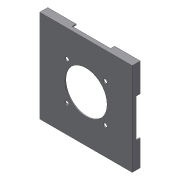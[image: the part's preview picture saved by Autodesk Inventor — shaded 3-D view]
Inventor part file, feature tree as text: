
AUTODESK INVENTOR PART (.ipt)
format: ipt  version: 2017 (Build 210142000, 142)  size: 223,744 bytes
history: native  units: mm
features: sketch x7, extrude x5, projected_geometry x3, hole x1, pattern_circular x1
ambient origin geometry x8: Origin, YZ Plane, XZ Plane, XY Plane, X Axis, Y Axis, Z Axis, Center Point
bodies: Solid1 (feature_tree)
feature tree (17):
  extrude  "Extrusion1"  Depth=90.0mm
  sketch  "Sketch2"  dims[d2=92.0mm d3=92.0mm]
  extrude  "Extrusion2"  Depth=92.0mm
  extrude  "Extrusion3"  Depth=90.0mm
  hole  "Hole1"  [1 undecoded]
  pattern_circular  "Circular Pattern2"  [2 undecoded]
  extrude  "Extrusion4"  Depth=17.25mm
  extrude  "Extrusion5"  Depth=7.0mm TaperAngle=0.0deg
  sketch  "Sketch1"  dims[d0=90.0mm d1=90.0mm]
  projected_geometry  "Projected Loop1"
  sketch  "Sketch3"  dims[d4=1.0mm d5=0.0mm d6=90.0mm]
  sketch  "Sketch4"  dims[d7=90.0mm d8=1.0mm]
  projected_geometry  "Projected Loop2"
  projected_geometry  "Projected Loop3"
  sketch  "Sketch5"  dims[d9=1.0mm]
  sketch  "Sketch6"  dims[d10=10.0mm]
  sketch  "Sketch7"  dims[d11=10.0mm d12=14.5mm d13=17.25mm d14=7.0mm d15=0.0mm d16=22.5mm d17=8.625mm d18=10.0mm d19=0.0mm d23=27.0mm d24=27.0mm d25=4.0mm d26=6.0mm d27=4.0mm d28=2.0mm d29=90.0deg d30=8.0mm d31=20.594885mm d32=40.0mm d33=360.0deg d35=42.0mm d36=10.0mm d37=0.0mm d38=90.0mm d39=90.0mm d40=3.0mm d41=0.0mm]
note: 3 required parameter values undecoded (feature->parameter linkage not recoverable at this tier; creation-order binding heuristic only, values carry confidence <= 0.55)
